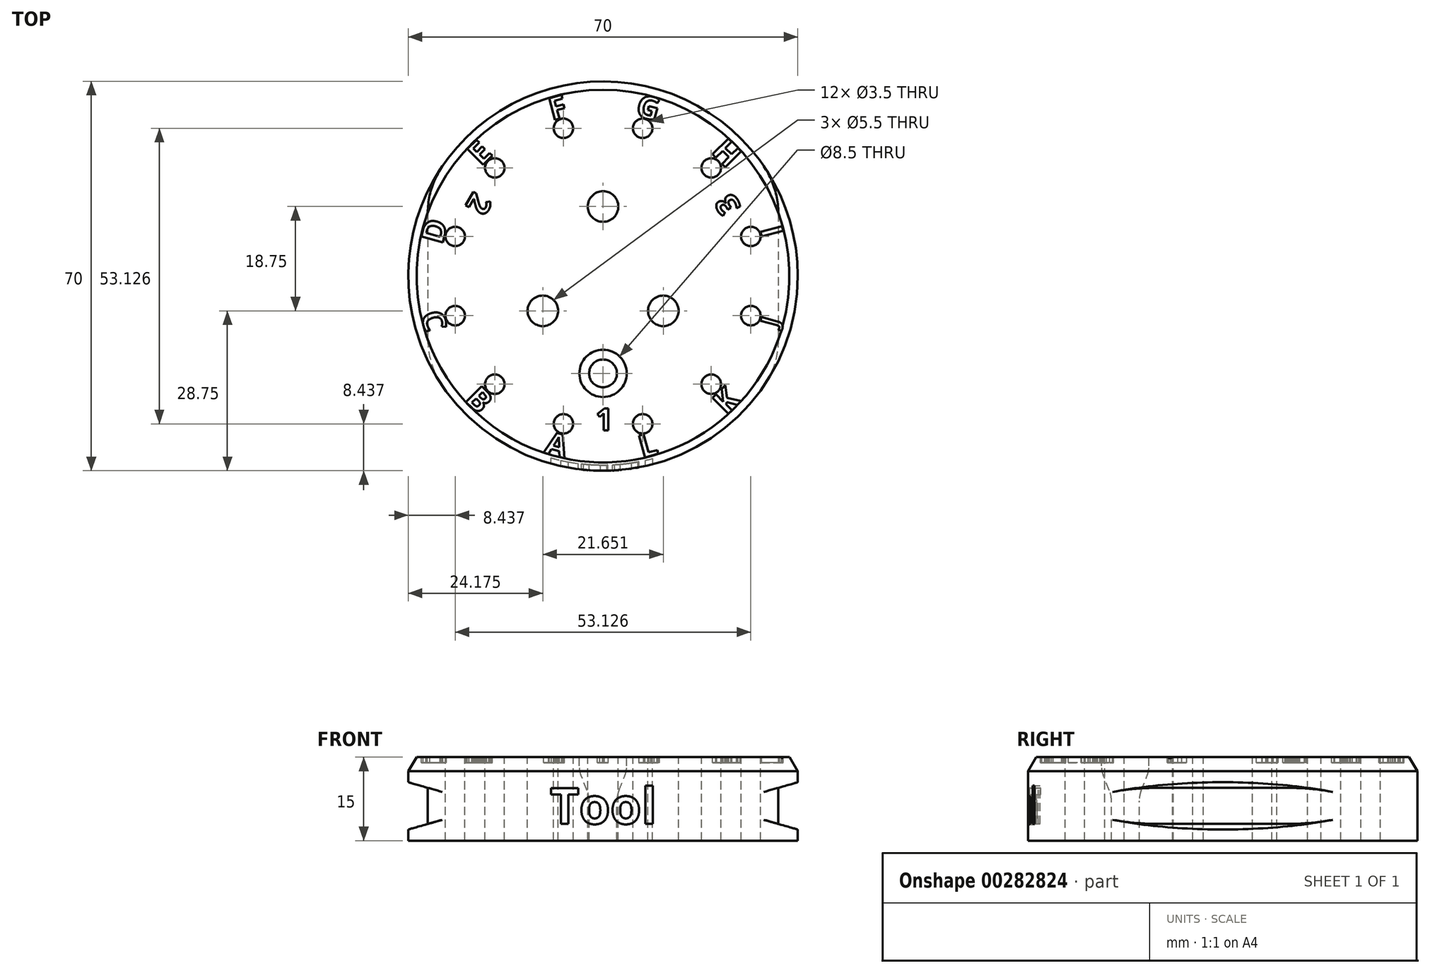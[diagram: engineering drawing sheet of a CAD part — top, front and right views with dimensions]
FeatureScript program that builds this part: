
annotation { "Feature Type Name" : "Feature", "Feature Type Description" : "" }
export const myFeature = defineFeature(function(context is Context, id is Id, definition is map)
    precondition{}
    {
        {
            var Q0;
            Q0=qCreatedBy(makeId("Top.planeOp"),FACE);
            var sketch = newSketch(context, id + "F0", { "sketchPlane" : qUnion([Q0])});
            skCircle(sketch, "E0", {"center": v(0, 0) * mm, "radius": 35 * mm});
            skSolve(sketch);
        }
        {
            var Q0;
            Q0=qSketchRegion(id+"F0",true);
            extrude(context, id + "F1", {"entities" : qUnion([Q0]), "depth" : 15 * mm});
        }
        {
            var Q0;
            Q0=qCreatedBy(makeId("Front.planeOp"),FACE);
            var sketch = newSketch(context, id + "F2", { "sketchPlane" : qUnion([Q0])});
            skText(sketch, "E1", { "text": "Tool", "fontName": "OpenSans-Bold.ttf"});
            const initialGuessF2  = {"E1": [-0.00952, 0.003, 1, 0, 0.0065]};
            skSetInitialGuess(sketch, initialGuessF2);
            skSolve(sketch);
        }
        {
            var Q0;
            Q0=qSketchRegion(id+"F2",true);
            var Q1;
            Q1=makeQuery(id+"F1.opExtrude","SWEPT_FACE",FACE,{"disambiguationData":[OSD([sQuery(id+"F0.wireOp",EDGE,"E0")])]});
            extrude(context, id + "F3", {"entities" : qUnion([Q0]), "operationType" : NewBodyOperationType.REMOVE, "endBound" : BoundingType.THROUGH_ALL, "endBoundEntityFace" : qUnion([Q1]), "depth" : 25 * mm});
        }
        {
            var Q0;
            Q0=makeQuery(id+"F1.opExtrude","CAP_FACE",FACE,{"disambiguationData":[OSD([sQuery(id+"F0.wireOp",EDGE,"E0")])],"isStart":false});
            var sketch = newSketch(context, id + "F4", { "sketchPlane" : qUnion([Q0])});
            skCircle(sketch, "E2", {"center": v(0, 0) * mm, "radius": 34 * mm});
            skSolve(sketch);
        }
        {
            var Q0;
            Q0=qSketchRegion(id+"F4",true);
            var Q1;
            Q1=makeQuery(id+"F1.opExtrude","CAP_FACE",FACE,{"disambiguationData":[OSD([sQuery(id+"F0.wireOp",EDGE,"E0")])],"isStart":true});
            extrude(context, id + "F5", {"entities" : qUnion([Q0]), "operationType" : NewBodyOperationType.ADD, "endBound" : BoundingType.UP_TO_SURFACE, "oppositeDirection" : true, "endBoundEntityFace" : qUnion([Q1]), "depth" : 25 * mm});
        }
        {
            var Q0;
            Q0=qCreatedBy(makeId("Front.planeOp"),FACE);
            var sketch = newSketch(context, id + "F6", { "sketchPlane" : qUnion([Q0])});
            skLineSegment(sketch, "E3", {"start": v(-35, 10.5) * mm, "end": v(-35, 2) * mm});
            skLineSegment(sketch, "E4", {"start": v(-35, 2) * mm, "end": v(-31.5, 3) * mm});
            skLineSegment(sketch, "E5", {"start": v(-31.5, 3) * mm, "end": v(-31.5, 9.5) * mm});
            skLineSegment(sketch, "E6", {"start": v(-31.5, 9.5) * mm, "end": v(-35, 10.5) * mm});
            skLineSegment(sketch, "E7.MirrorCS", {"start": v(35, 10.5) * mm, "end": v(35, 2) * mm});
            skLineSegment(sketch, "E8.MirrorCS", {"start": v(31.5, 9.5) * mm, "end": v(35, 10.5) * mm});
            skLineSegment(sketch, "E9.MirrorCS", {"start": v(35, 2) * mm, "end": v(31.5, 3) * mm});
            skLineSegment(sketch, "E10.MirrorCS", {"start": v(31.5, 3) * mm, "end": v(31.5, 9.5) * mm});
            skSolve(sketch);
        }
        {
            var Q0;
            Q0=qSketchRegion(id+"F6",true);
            extrude(context, id + "F7", {"entities" : qUnion([Q0]), "operationType" : NewBodyOperationType.REMOVE, "endBound" : BoundingType.THROUGH_ALL, "oppositeDirection" : true, "depth" : 25 * mm, "hasSecondDirection" : true, "secondDirectionBound" : SecondDirectionBoundingType.THROUGH_ALL, "secondDirectionOppositeDirection" : false, "secondDirectionDepth" : 25 * mm});
        }
        {
            var Q0;
            {var subQ0=sQuery(id+"F0.wireOp",EDGE,"E0");Q0=makeQuery(id+"F7.boolean.opBoolean","INTERSECT",EDGE,{"disambiguationData":[OD(0.0)],"derivedFrom":[makeQuery(id+"F3.boolean.opBoolean","SPLIT",FACE,{"disambiguationData":[TD([makeQuery(id+"F1.opExtrude","CAP_FACE",FACE,{"disambiguationData":[OSD([subQ0])],"isStart":true})])],"derivedFrom":makeQuery(id+"F1.opExtrude","SWEPT_FACE",FACE,{"disambiguationData":[OSD([subQ0])]})}),makeQuery(id+"F7.opExtrude","SWEPT_FACE",FACE,{"disambiguationData":[OSD([sQuery(id+"F6.wireOp",EDGE,"E5")])]})]});}
            var Q1;
            {var subQ0=sQuery(id+"F0.wireOp",EDGE,"E0");Q1=makeQuery(id+"F7.boolean.opBoolean","INTERSECT",EDGE,{"disambiguationData":[OD(0.0)],"derivedFrom":[makeQuery(id+"F3.boolean.opBoolean","SPLIT",FACE,{"disambiguationData":[TD([makeQuery(id+"F1.opExtrude","CAP_FACE",FACE,{"disambiguationData":[OSD([subQ0])],"isStart":true})])],"derivedFrom":makeQuery(id+"F1.opExtrude","SWEPT_FACE",FACE,{"disambiguationData":[OSD([subQ0])]})}),makeQuery(id+"F7.opExtrude","SWEPT_FACE",FACE,{"disambiguationData":[OSD([sQuery(id+"F6.wireOp",EDGE,"E10.MirrorCS")])]})]});}
            var Q2;
            {var subQ0=sQuery(id+"F0.wireOp",EDGE,"E0");Q2=makeQuery(id+"F7.boolean.opBoolean","INTERSECT",EDGE,{"disambiguationData":[OD(1.0)],"derivedFrom":[makeQuery(id+"F3.boolean.opBoolean","SPLIT",FACE,{"disambiguationData":[TD([makeQuery(id+"F1.opExtrude","CAP_FACE",FACE,{"disambiguationData":[OSD([subQ0])],"isStart":true})])],"derivedFrom":makeQuery(id+"F1.opExtrude","SWEPT_FACE",FACE,{"disambiguationData":[OSD([subQ0])]})}),makeQuery(id+"F7.opExtrude","SWEPT_FACE",FACE,{"disambiguationData":[OSD([sQuery(id+"F6.wireOp",EDGE,"E10.MirrorCS")])]})]});}
            var Q3;
            {var subQ0=sQuery(id+"F0.wireOp",EDGE,"E0");Q3=makeQuery(id+"F7.boolean.opBoolean","INTERSECT",EDGE,{"disambiguationData":[OD(1.0)],"derivedFrom":[makeQuery(id+"F3.boolean.opBoolean","SPLIT",FACE,{"disambiguationData":[TD([makeQuery(id+"F1.opExtrude","CAP_FACE",FACE,{"disambiguationData":[OSD([subQ0])],"isStart":true})])],"derivedFrom":makeQuery(id+"F1.opExtrude","SWEPT_FACE",FACE,{"disambiguationData":[OSD([subQ0])]})}),makeQuery(id+"F7.opExtrude","SWEPT_FACE",FACE,{"disambiguationData":[OSD([sQuery(id+"F6.wireOp",EDGE,"E5")])]})]});}
            fillet(context, id + "F8", {"entities" : qUnion([Q0, Q1, Q2, Q3]), "radius" : 15 * mm, "tangentPropagation" : true, "allowEdgeOverflow" : false});
        }
        {
            var Q0;
            Q0=makeQuery(id+"F1.opExtrude","CAP_FACE",FACE,{"disambiguationData":[OSD([sQuery(id+"F0.wireOp",EDGE,"E0")])],"isStart":false});
            var sketch = newSketch(context, id + "F9", { "sketchPlane" : qUnion([Q0])});
            skCircle(sketch, "E11", {"center": v(0, 12.5) * mm, "radius": 2.75 * mm});
            skCircle(sketch, "E12.1.0", {"center": v(-10.83, -6.25) * mm, "radius": 2.75 * mm});
            skCircle(sketch, "E12.2.0", {"center": v(10.83, -6.25) * mm, "radius": 2.75 * mm});
            skPoint(sketch, "E12.center", {"position": v(0, 0) * mm});
            skCircle(sketch, "E13", {"center": v(0, 0) * mm, "radius": 12.5 * mm, "construction": true});
            skSolve(sketch);
        }
        {
            var Q0;
            Q0=qSketchRegion(id+"F9",true);
            extrude(context, id + "F10", {"entities" : qUnion([Q0]), "operationType" : NewBodyOperationType.REMOVE, "endBound" : BoundingType.THROUGH_ALL, "oppositeDirection" : true, "depth" : 25 * mm});
        }
        {
            var Q0;
            Q0=makeQuery(id+"F1.opExtrude","CAP_FACE",FACE,{"disambiguationData":[OSD([sQuery(id+"F0.wireOp",EDGE,"E0")])],"isStart":false});
            var sketch = newSketch(context, id + "F11", { "sketchPlane" : qUnion([Q0])});
            skCircle(sketch, "E14", {"center": v(0, -17.5) * mm, "radius": 2.5 * mm});
            skCircle(sketch, "E15", {"center": v(0, 0) * mm, "radius": 17.5 * mm, "construction": true});
            skSolve(sketch);
        }
        {
            var Q0;
            Q0=qSketchRegion(id+"F11",true);
            extrude(context, id + "F12", {"entities" : qUnion([Q0]), "operationType" : NewBodyOperationType.REMOVE, "endBound" : BoundingType.THROUGH_ALL, "oppositeDirection" : true, "depth" : 25 * mm});
        }
        {
            var Q0;
            Q0=makeQuery(id+"F1.opExtrude","CAP_FACE",FACE,{"disambiguationData":[OSD([sQuery(id+"F0.wireOp",EDGE,"E0")])],"isStart":false});
            var sketch = newSketch(context, id + "F13", { "sketchPlane" : qUnion([Q0])});
            skCircle(sketch, "E16", {"center": v(0, -17.5) * mm, "radius": 4.25 * mm});
            skSolve(sketch);
        }
        {
            var Q0;
            Q0=qSketchRegion(id+"F13",true);
            extrude(context, id + "F14", {"entities" : qUnion([Q0]), "operationType" : NewBodyOperationType.REMOVE, "oppositeDirection" : true, "depth" : 7.5 * mm});
        }
        {
            var Q0;
            Q0=makeQuery(id+"F14.boolean.opBoolean","COPY",EDGE,{"derivedFrom":makeQuery(id+"F14.opExtrude","CAP_EDGE",EDGE,{"disambiguationData":[OSD([sQuery(id+"F13.wireOp",EDGE,"E16")])],"isStart":false})});
            chamfer(context, id + "F15", {"entities" : qUnion([Q0]), "chamferType" : ChamferType.TWO_OFFSETS, "width1" : 5 * mm, "oppositeDirection" : true, "width2" : 2 * mm, "tangentPropagation" : true});
        }
        {
            var Q0;
            {var subQ0=sQuery(id+"F13.wireOp",EDGE,"E16");Q0=makeQuery(id+"F15.opChamfer","BLEND_EDGE",EDGE,{"blendedFrom":[makeQuery(id+"F14.boolean.opBoolean","COPY",EDGE,{"derivedFrom":makeQuery(id+"F14.opExtrude","CAP_EDGE",EDGE,{"disambiguationData":[OSD([subQ0])],"isStart":false})}),makeQuery(id+"F14.boolean.opBoolean","COPY",FACE,{"derivedFrom":makeQuery(id+"F14.opExtrude","SWEPT_FACE",FACE,{"disambiguationData":[OSD([subQ0])]})})],"blendedInto":[makeQuery(id+"F14.boolean.opBoolean","COPY",FACE,{"derivedFrom":makeQuery(id+"F14.opExtrude","SWEPT_FACE",FACE,{"disambiguationData":[OSD([subQ0])]})})]});}
            var Q1;
            Q1=makeQuery(id+"F15.opChamfer","BLEND_EDGE",EDGE,{"blendedFrom":[makeQuery(id+"F14.boolean.opBoolean","COPY",EDGE,{"derivedFrom":makeQuery(id+"F14.opExtrude","CAP_EDGE",EDGE,{"disambiguationData":[OSD([sQuery(id+"F13.wireOp",EDGE,"E16")])],"isStart":false})}),makeQuery(id+"F12.boolean.opBoolean","COPY",FACE,{"derivedFrom":makeQuery(id+"F12.opExtrude","SWEPT_FACE",FACE,{"disambiguationData":[OSD([sQuery(id+"F11.wireOp",EDGE,"E14")])]})})],"blendedInto":[makeQuery(id+"F12.boolean.opBoolean","COPY",FACE,{"derivedFrom":makeQuery(id+"F12.opExtrude","SWEPT_FACE",FACE,{"disambiguationData":[OSD([sQuery(id+"F11.wireOp",EDGE,"E14")])]})})]});
            fillet(context, id + "F16", {"entities" : qUnion([Q0, Q1]), "radius" : 5 * mm, "tangentPropagation" : true, "allowEdgeOverflow" : false});
        }
        {
            var Q0;
            Q0=makeQuery(id+"F1.opExtrude","CAP_FACE",FACE,{"disambiguationData":[OSD([sQuery(id+"F0.wireOp",EDGE,"E0")])],"isStart":false});
            var sketch = newSketch(context, id + "F17", { "sketchPlane" : qUnion([Q0])});
            skCircle(sketch, "E17", {"center": v(19.45, 19.45) * mm, "radius": 1.75 * mm});
            skCircle(sketch, "E18", {"center": v(0, 0) * mm, "radius": 27.5 * mm, "construction": true});
            skLineSegment(sketch, "E19", {"start": v(0, 0) * mm, "end": v(19.45, 19.45) * mm, "construction": true});
            skCircle(sketch, "E20.1.1", {"center": v(7.12, 26.56) * mm, "radius": 1.75 * mm});
            skCircle(sketch, "E20.2.1", {"center": v(-7.12, 26.56) * mm, "radius": 1.75 * mm});
            skCircle(sketch, "E20.3.1", {"center": v(-19.45, 19.45) * mm, "radius": 1.75 * mm});
            skCircle(sketch, "E20.4.1", {"center": v(-26.56, 7.12) * mm, "radius": 1.75 * mm});
            skCircle(sketch, "E20.5.1", {"center": v(-26.56, -7.12) * mm, "radius": 1.75 * mm});
            skCircle(sketch, "E20.6.1", {"center": v(-19.45, -19.45) * mm, "radius": 1.75 * mm});
            skCircle(sketch, "E20.7.1", {"center": v(-7.12, -26.56) * mm, "radius": 1.75 * mm});
            skCircle(sketch, "E20.8.1", {"center": v(7.12, -26.56) * mm, "radius": 1.75 * mm});
            skCircle(sketch, "E20.9.1", {"center": v(19.45, -19.45) * mm, "radius": 1.75 * mm});
            skCircle(sketch, "E20.10.1", {"center": v(26.56, -7.12) * mm, "radius": 1.75 * mm});
            skCircle(sketch, "E20.11.1", {"center": v(26.56, 7.12) * mm, "radius": 1.75 * mm});
            skSolve(sketch);
        }
        {
            var Q0;
            Q0=qSketchRegion(id+"F17",true);
            extrude(context, id + "F18", {"entities" : qUnion([Q0]), "operationType" : NewBodyOperationType.REMOVE, "endBound" : BoundingType.THROUGH_ALL, "oppositeDirection" : true, "depth" : 25 * mm});
        }
        {
            var Q0;
            Q0=makeQuery(id+"F1.opExtrude","CAP_EDGE",EDGE,{"disambiguationData":[OSD([sQuery(id+"F0.wireOp",EDGE,"E0")])],"isStart":false});
            chamfer(context, id + "F19", {"entities" : qUnion([Q0]), "chamferType" : ChamferType.TWO_OFFSETS, "width1" : 2.5 * mm, "oppositeDirection" : true, "width2" : 1.5 * mm, "tangentPropagation" : true});
        }
        {
            var Q0;
            Q0=makeQuery(id+"F1.opExtrude","CAP_FACE",FACE,{"disambiguationData":[OSD([sQuery(id+"F0.wireOp",EDGE,"E0")])],"isStart":false});
            var sketch = newSketch(context, id + "F20", { "sketchPlane" : qUnion([Q0])});
            skText(sketch, "E21", { "text": "A", "fontName": "OpenSans-Bold.ttf"});
            skText(sketch, "E22", { "text": "B", "fontName": "OpenSans-Bold.ttf"});
            skText(sketch, "E23", { "text": "C", "fontName": "OpenSans-Bold.ttf"});
            skText(sketch, "E24", { "text": "E", "fontName": "OpenSans-Bold.ttf"});
            skText(sketch, "E25", { "text": "F", "fontName": "OpenSans-Bold.ttf"});
            skText(sketch, "E26", { "text": "G", "fontName": "OpenSans-Bold.ttf"});
            skText(sketch, "E27", { "text": "H", "fontName": "OpenSans-Bold.ttf"});
            skText(sketch, "E28", { "text": "I", "fontName": "OpenSans-Bold.ttf"});
            skText(sketch, "E29", { "text": "J", "fontName": "OpenSans-Bold.ttf"});
            skText(sketch, "E30", { "text": "K", "fontName": "OpenSans-Bold.ttf"});
            skText(sketch, "E31", { "text": "L", "fontName": "OpenSans-Bold.ttf"});
            skText(sketch, "E32", { "text": "D", "fontName": "OpenSans-Bold.ttf"});
            skCircle(sketch, "E33", {"center": v(0, 0) * mm, "radius": 29.38 * mm, "construction": true});
            skText(sketch, "E34", { "text": "1", "fontName": "OpenSans-Bold.ttf"});
            skText(sketch, "E35", { "text": "2", "fontName": "OpenSans-Bold.ttf"});
            skText(sketch, "E36", { "text": "3", "fontName": "OpenSans-Bold.ttf"});
            skCircle(sketch, "E37", {"center": v(0, 0) * mm, "radius": 23.75 * mm, "construction": true});
            const initialGuessF20  = {"E21": [-0.0107, -0.03174, 0.96593, -0.25882, 0.00406], "E22": [-0.025, -0.02228, 0.7071, -0.7071, 0.00406], "E23": [-0.03278, -0.00684, 0.25882, -0.96593, 0.00406], "E24": [-0.0219, 0.01964, 0.7071, 0.7071, 0.00406], "E25": [-0.00914, 0.02796, 0.96593, 0.25882, 0.00406], "E26": [0.00567, 0.0289, 0.96593, -0.25882, 0.00406], "E27": [0.0193, 0.02225, 0.7071, -0.7071, 0.00406], "E28": [0.02815, 0.00844, 0.25882, -0.96593, 0.00406], "E29": [0.0313, -0.00927, 0.25882, 0.96593, 0.00325], "E30": [0.02219, -0.0251, 0.7071, 0.7071, 0.00406], "E31": [0.00703, -0.03273, 0.96593, 0.25882, 0.00406], "E32": [-0.02892, 0.00557, 0.25882, 0.96593, 0.00406], "E34": [-0.00133, -0.02775, 1, 0, 0.004], "E35": [-0.0232, 0.01533, -0.5, -0.86603, 0.004], "E36": [0.02486, 0.01244, -0.5, 0.86603, 0.004]};
            skSetInitialGuess(sketch, initialGuessF20);
            skSolve(sketch);
        }
        {
            var Q0;
            Q0=qSketchRegion(id+"F20",true);
            extrude(context, id + "F21", {"entities" : qUnion([Q0]), "operationType" : NewBodyOperationType.REMOVE, "oppositeDirection" : true, "depth" : 1 * mm});
        }
    });
